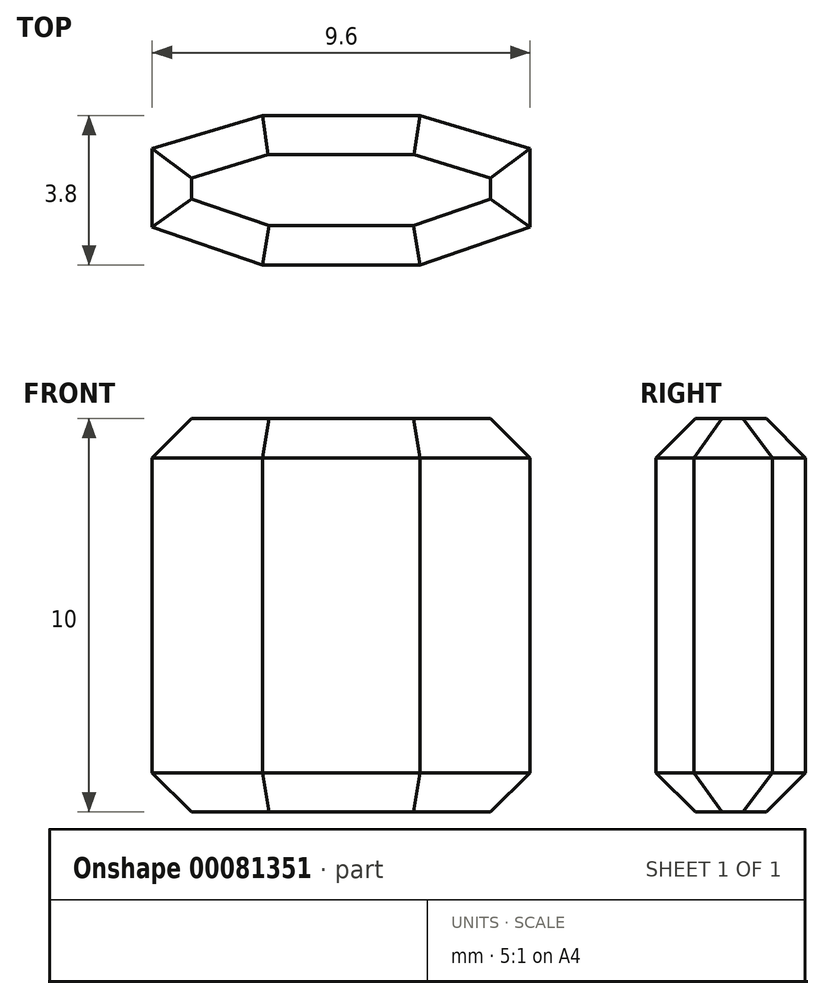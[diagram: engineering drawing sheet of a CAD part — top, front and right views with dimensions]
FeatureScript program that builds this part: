
annotation { "Feature Type Name" : "Feature", "Feature Type Description" : "" }
export const myFeature = defineFeature(function(context is Context, id is Id, definition is map)
    precondition{}
    {
        {
            var Q0;
            Q0=qCreatedBy(makeId("Top.planeOp"),FACE);
            var sketch = newSketch(context, id + "F0", { "sketchPlane" : qUnion([Q0])});
            skLineSegment(sketch, "E0.bottom", {"start": v(4.8, 1.9) * mm, "end": v(-4.8, 1.9) * mm, "construction": true});
            skLineSegment(sketch, "E0.top", {"start": v(4.8, -1.9) * mm, "end": v(-4.8, -1.9) * mm, "construction": true});
            skLineSegment(sketch, "E0.left", {"start": v(4.8, 1.9) * mm, "end": v(4.8, -1.9) * mm, "construction": true});
            skLineSegment(sketch, "E0.right", {"start": v(-4.8, 1.9) * mm, "end": v(-4.8, -1.9) * mm, "construction": true});
            skPoint(sketch, "E0.middle", {"position": v(0, 0) * mm});
            skLineSegment(sketch, "E1", {"start": v(-4.8, 1.06) * mm, "end": v(-2, 1.9) * mm});
            skLineSegment(sketch, "E2", {"start": v(-4.8, 1.06) * mm, "end": v(-4.8, -0.94) * mm});
            skLineSegment(sketch, "E3", {"start": v(-4.8, -0.94) * mm, "end": v(-2, -1.9) * mm});
            skLineSegment(sketch, "E4", {"start": v(-2, -1.9) * mm, "end": v(2, -1.9) * mm});
            skLineSegment(sketch, "E5", {"start": v(2, -1.9) * mm, "end": v(4.8, -0.94) * mm});
            skLineSegment(sketch, "E6", {"start": v(4.8, -0.94) * mm, "end": v(4.8, 1.06) * mm});
            skLineSegment(sketch, "E7", {"start": v(4.8, 1.06) * mm, "end": v(2, 1.9) * mm});
            skLineSegment(sketch, "E8", {"start": v(2, 1.9) * mm, "end": v(-2, 1.9) * mm});
            skSolve(sketch);
        }
        {
            var Q0;
            Q0 = qSketchRegion(id + "F0", true);
            extrude(context, id + "F1", {"entities" : qUnion([Q0]), "depth" : 10 * mm});
        }
        {
            var Q0;
            Q0=makeQuery(id+"F1.opExtrude","CAP_EDGE",EDGE,{"disambiguationData":[OSD([sQuery(id+"F0.wireOp",EDGE,"E8")])],"isStart":false});
            var Q1;
            Q1=makeQuery(id+"F1.opExtrude","CAP_EDGE",EDGE,{"disambiguationData":[OSD([sQuery(id+"F0.wireOp",EDGE,"E4")])],"isStart":false});
            var Q2;
            Q2=makeQuery(id+"F1.opExtrude","CAP_EDGE",EDGE,{"disambiguationData":[OSD([sQuery(id+"F0.wireOp",EDGE,"E2")])],"isStart":false});
            var Q3;
            Q3=makeQuery(id+"F1.opExtrude","CAP_EDGE",EDGE,{"disambiguationData":[OSD([sQuery(id+"F0.wireOp",EDGE,"E6")])],"isStart":false});
            var Q4;
            Q4=makeQuery(id+"F1.opExtrude","CAP_EDGE",EDGE,{"disambiguationData":[OSD([sQuery(id+"F0.wireOp",EDGE,"E7")])],"isStart":false});
            var Q5;
            Q5=makeQuery(id+"F1.opExtrude","CAP_EDGE",EDGE,{"disambiguationData":[OSD([sQuery(id+"F0.wireOp",EDGE,"E1")])],"isStart":false});
            var Q6;
            Q6=makeQuery(id+"F1.opExtrude","CAP_EDGE",EDGE,{"disambiguationData":[OSD([sQuery(id+"F0.wireOp",EDGE,"E3")])],"isStart":false});
            var Q7;
            Q7=makeQuery(id+"F1.opExtrude","CAP_EDGE",EDGE,{"disambiguationData":[OSD([sQuery(id+"F0.wireOp",EDGE,"E5")])],"isStart":false});
            var Q8;
            Q8=makeQuery(id+"F1.opExtrude","CAP_EDGE",EDGE,{"disambiguationData":[OSD([sQuery(id+"F0.wireOp",EDGE,"E8")])],"isStart":true});
            var Q9;
            Q9=makeQuery(id+"F1.opExtrude","CAP_EDGE",EDGE,{"disambiguationData":[OSD([sQuery(id+"F0.wireOp",EDGE,"E1")])],"isStart":true});
            var Q10;
            Q10=makeQuery(id+"F1.opExtrude","CAP_EDGE",EDGE,{"disambiguationData":[OSD([sQuery(id+"F0.wireOp",EDGE,"E2")])],"isStart":true});
            var Q11;
            Q11=makeQuery(id+"F1.opExtrude","CAP_EDGE",EDGE,{"disambiguationData":[OSD([sQuery(id+"F0.wireOp",EDGE,"E3")])],"isStart":true});
            var Q12;
            Q12=makeQuery(id+"F1.opExtrude","CAP_EDGE",EDGE,{"disambiguationData":[OSD([sQuery(id+"F0.wireOp",EDGE,"E4")])],"isStart":true});
            var Q13;
            Q13=makeQuery(id+"F1.opExtrude","CAP_EDGE",EDGE,{"disambiguationData":[OSD([sQuery(id+"F0.wireOp",EDGE,"E5")])],"isStart":true});
            var Q14;
            Q14=makeQuery(id+"F1.opExtrude","CAP_EDGE",EDGE,{"disambiguationData":[OSD([sQuery(id+"F0.wireOp",EDGE,"E6")])],"isStart":true});
            var Q15;
            Q15=makeQuery(id+"F1.opExtrude","CAP_EDGE",EDGE,{"disambiguationData":[OSD([sQuery(id+"F0.wireOp",EDGE,"E7")])],"isStart":true});
            chamfer(context, id + "F2", {"entities" : qUnion([Q0, Q1, Q2, Q3, Q4, Q5, Q6, Q7, Q8, Q9, Q10, Q11, Q12, Q13, Q14, Q15]), "width" : 1 * mm, "tangentPropagation" : true});
        }
        {
            var Q0;
            Q0=makeQuery(id+"F1.opExtrude","SWEPT_BODY",BODY,{"disambiguationData":[OSD([sQuery(id+"F0.wireOp",EDGE,"E1"),sQuery(id+"F0.wireOp",EDGE,"E2"),sQuery(id+"F0.wireOp",EDGE,"E3"),sQuery(id+"F0.wireOp",EDGE,"E4"),sQuery(id+"F0.wireOp",EDGE,"E5"),sQuery(id+"F0.wireOp",EDGE,"E6"),sQuery(id+"F0.wireOp",EDGE,"E7"),sQuery(id+"F0.wireOp",EDGE,"E8")])]});
            transform(context, id + "F3", {"entities" : qUnion([Q0]), "transformType" : TransformType.TRANSLATION_3D, "dx" : 0 * mm, "dy" : 0 * mm, "dz" : 0 * mm, "makeCopy" : true});
        }
    });
